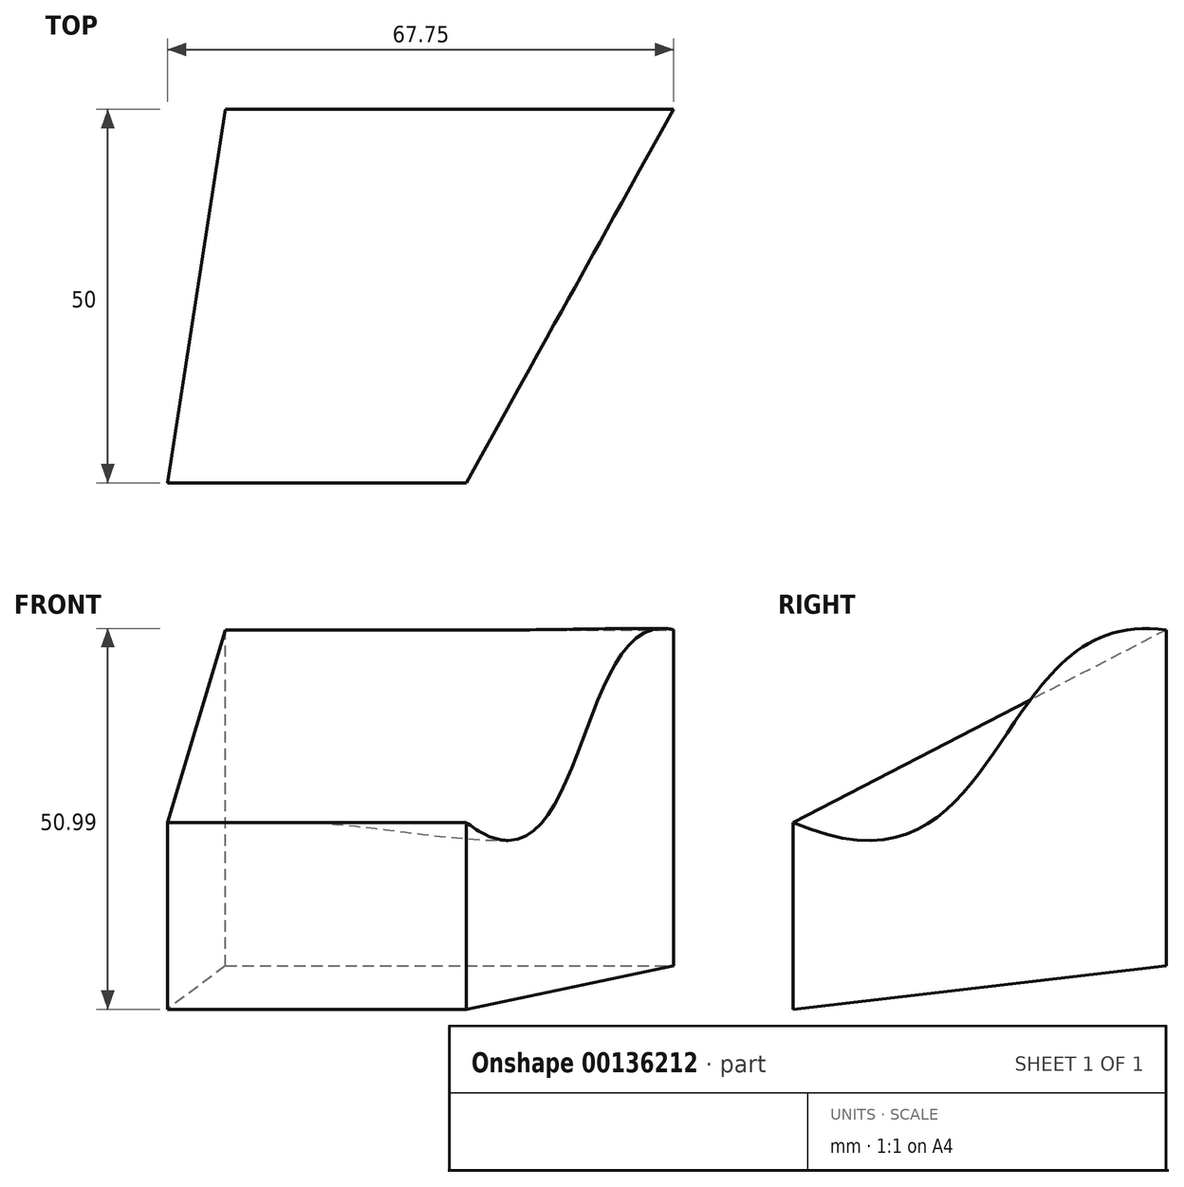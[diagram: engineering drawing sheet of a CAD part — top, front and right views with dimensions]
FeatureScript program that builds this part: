
annotation { "Feature Type Name" : "Feature", "Feature Type Description" : "" }
export const myFeature = defineFeature(function(context is Context, id is Id, definition is map)
    precondition{}
    {
        {
            var Q0;
            Q0=qCreatedBy(makeId("Front.planeOp"),FACE);
            var sketch = newSketch(context, id + "F0", { "sketchPlane" : qUnion([Q0])});
            skLineSegment(sketch, "E0.bottom", {"start": v(0, 0) * mm, "end": v(60, 0) * mm});
            skLineSegment(sketch, "E0.top", {"start": v(0, 45) * mm, "end": v(60, 45) * mm});
            skLineSegment(sketch, "E0.left", {"start": v(0, 0) * mm, "end": v(0, 45) * mm});
            skLineSegment(sketch, "E0.right", {"start": v(60, 0) * mm, "end": v(60, 45) * mm});
            skSolve(sketch);
        }
        {
            var Q0;
            Q0=qCreatedBy(makeId("Front.planeOp"),FACE);
            cPlane(context, id + "F1", {"entities" : qUnion([Q0]), "cplaneType" : CPlaneType.OFFSET, "offset" : 50 * mm, "width" : 150 * mm, "height" : 150 * mm});
        }
        {
            var Q0;
            Q0=qCreatedBy(id+"F1.planeOp",FACE);
            var sketch = newSketch(context, id + "F2", { "sketchPlane" : qUnion([Q0])});
            skLineSegment(sketch, "E1.bottom", {"start": v(-7.75, -5.8) * mm, "end": v(32.25, -5.8) * mm});
            skLineSegment(sketch, "E1.top", {"start": v(-7.75, 19.2) * mm, "end": v(32.25, 19.2) * mm});
            skLineSegment(sketch, "E1.left", {"start": v(-7.75, -5.8) * mm, "end": v(-7.75, 19.2) * mm});
            skLineSegment(sketch, "E1.right", {"start": v(32.25, -5.8) * mm, "end": v(32.25, 19.2) * mm});
            skSolve(sketch);
        }
        {
            var Q0;
            Q0=sQuery(id+"F0.wireOp",VERTEX,"E0.right.end");
            var Q1;
            Q1=sQuery(id+"F0.wireOp",VERTEX,"E0.bottom.end");
            var Q2;
            Q2=sQuery(id+"F2.wireOp",VERTEX,"E1.bottom.end");
            cPlane(context, id + "F3", {"entities" : qUnion([Q0, Q1, Q2]), "cplaneType" : CPlaneType.THREE_POINT, "offset" : 25 * mm, "width" : 150 * mm, "height" : 150 * mm});
        }
        {
            var Q0;
            Q0=qCreatedBy(id+"F3.planeOp",FACE);
            var sketch = newSketch(context, id + "F4", { "sketchPlane" : qUnion([Q0])});
            skFitSpline(sketch, "E2", {"points": [v(-28.07, 19.2) * mm, v(29.12, 45) * mm], "startDerivative": vector(100.52, -38.08) * mm, "endDerivative": vector(83.07, -9.98) * mm});
            skSolve(sketch);
        }
        {
            var Q0;
            Q0=makeQuery(id+"F0.imprint","IMPRINT",FACE,{"disambiguationData":[TD([[makeQuery(id+"F0.imprint","IMPRINT",EDGE,{"derivedFrom":sQuery(id+"F0.wireOp",EDGE,"E0.bottom")}),1.0]])]});
            var Q1;
            Q1=makeQuery(id+"F2.imprint","IMPRINT",FACE,{"disambiguationData":[TD([[makeQuery(id+"F2.imprint","IMPRINT",EDGE,{"derivedFrom":sQuery(id+"F2.wireOp",EDGE,"E1.bottom")}),1.0]])]});
            var Q2;
            Q2=sQuery(id+"F4.wireOp",EDGE,"E2");
            loft(context, id + "F5", {"addGuides" : true, "sheetProfilesArray" : [{ "sheetProfileEntities" : qUnion([Q0]) }, { "sheetProfileEntities" : qUnion([Q1]) }], "guidesArray" : [{ "guideEntities" : qUnion([Q2]), "guideDerivativeType" : LoftGuideDerivativeType.DEFAULT, "guideDerivativeMagnitude" : 1 }]});
        }
    });
